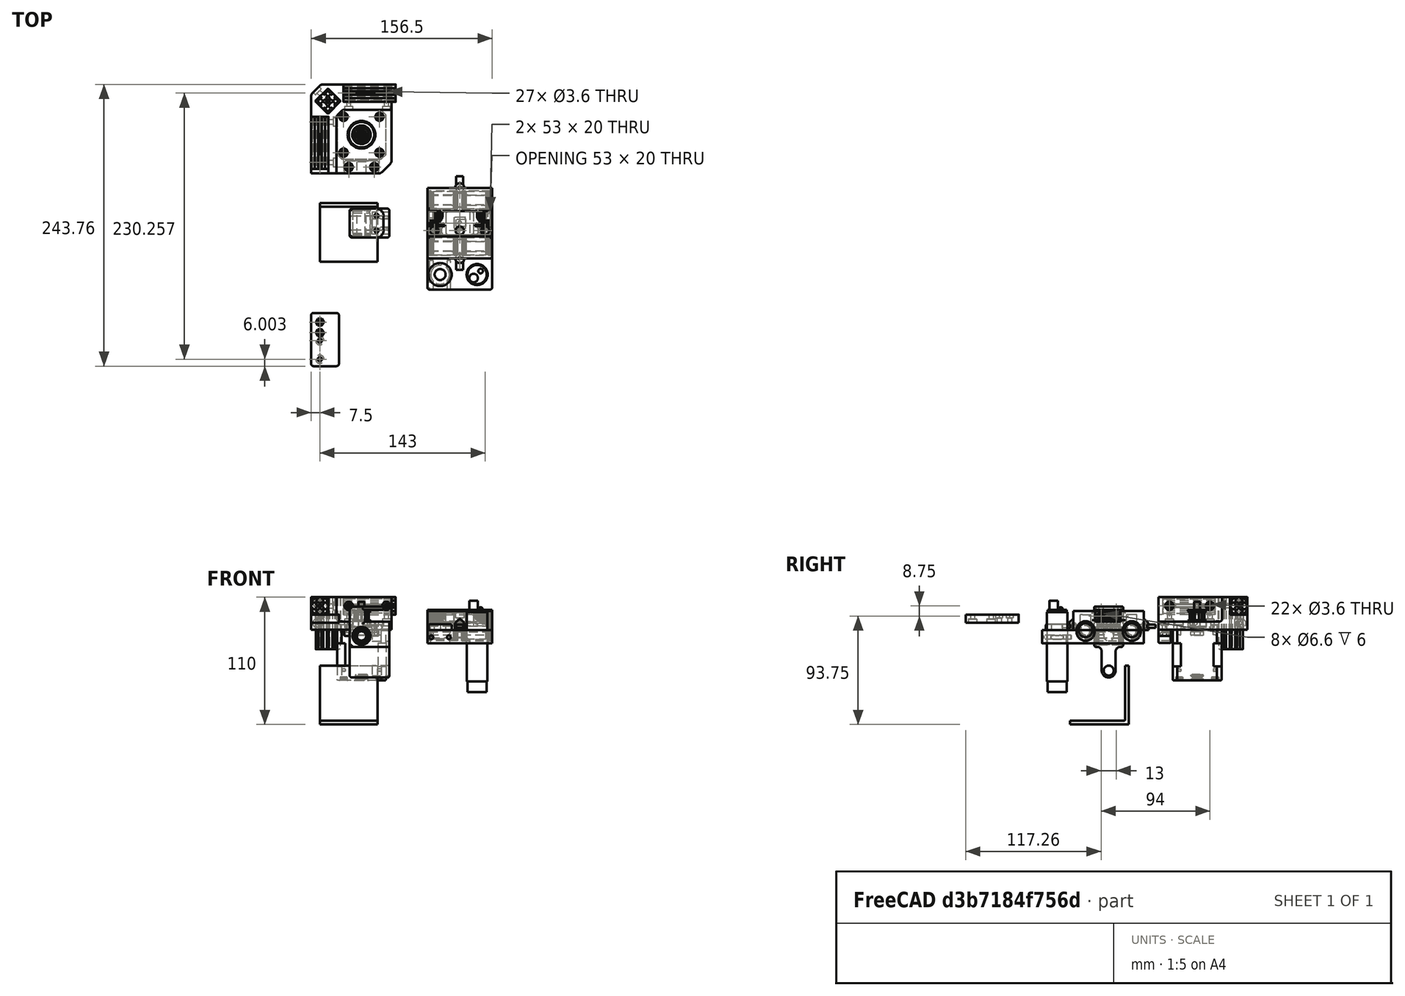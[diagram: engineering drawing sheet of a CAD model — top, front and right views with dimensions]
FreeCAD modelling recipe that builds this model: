
FCSTD DOCUMENT  (FreeCAD 0.15R4671 (Git))
Label: XCarrageTop
License: All rights reserved
LicenseURL: http://en.wikipedia.org/wiki/All_rights_reserved
objects: Sketcher::SketchObject×26, Mesh::Feature×24, Part::Feature×21, PartDesign::Pocket×20, PartDesign::Fillet×10, PartDesign::Pad×6, PartDesign::Chamfer×2
note: 111 computed .brp shape members not serialized (recipe doc carries the construction recipe); baked Part::Feature solids carry a one-line shape summary decoded from their .brp

FEATURE [Part::Feature] Part__Feature  label="OB1515_45mm001"
  Placement = pos=(0,79.5,22.5) rot=(1,0,0;1.5708rad)
  shape: bbox 15 x 45 x 15 mm, 158 faces (baked)
FEATURE [Part::Feature] Part__Feature001  label="OB1515_45mm"
  Placement = pos=(7,93,-15) rot=(0,0,1;0.785398rad)
  shape: bbox 21.01 x 21.01 x 45 mm, 158 faces (baked)
FEATURE [Part::Feature] Part__Feature002  label="OB1515_45mm002"
  Placement = pos=(20.5,100,22.5) rot=(0.57735,0.57735,0.57735;2.0944rad)
  shape: bbox 45 x 15 x 15 mm, 158 faces (baked)
FEATURE [Part::Feature] Part__Feature003  label="NEMA17"
  Placement = pos=(36,64,2) rot=(0,0,1;0rad)
  shape: bbox 42.3 x 42.3 x 68 mm, 275 faces (baked)
FEATURE [Part::Feature] Part__Feature004  label="T5_Pulley"
  Placement = pos=(36,64,-4) rot=(0,0,1;0rad)
  shape: bbox 16 x 16 x 14.8 mm, 116 faces (baked)
FEATURE [Mesh::Feature] _08ZZ_Ball_Bearing  label="608ZZ_Ball_Bearing001"
  Placement = pos=(54.5,64,25.1) rot=(0,0,1;0rad)
FEATURE [Mesh::Feature] Spacer
  Placement = pos=(21.5,54,17.6) rot=(0,0,1;0rad)
FEATURE [Mesh::Feature] _mmRod_x100mm  label="8mmRod_x100mm"
  Placement = pos=(36,-64.5,-3.5) rot=(0,0,1;3.14159rad)
FEATURE [Part::Feature] Part__Feature005  label="TopCornerMotor"
  Placement = pos=(0,100,0) rot=(0,0,1;0rad)
  shape: bbox 69.55 x 77 x 28 mm, 82 faces (baked)
FEATURE [Part::Feature] Part__Feature006  label="TopRodHolder"
  Placement = pos=(0,100,2) rot=(0,0,1;0rad)
  shape: bbox 30.16 x 11.33 x 11.99 mm, 58 faces (baked)
FEATURE [Part::Feature] LM8UU_8mm_Linear_Bearing001
  Placement = pos=(36,-24.5,-3.5) rot=(0,0,1;1.5708rad)
  shape: bbox 15 x 24 x 15 mm, 34 faces (baked)
FEATURE [Mesh::Feature] _mmRod_x100mm001  label="8mmRod_x100mm001"
  Placement = pos=(45,7.5,1.5) rot=(0,0,1;1.5708rad)
FEATURE [Mesh::Feature] _mmRod_x100mm002  label="8mmRod_x100mm002"
  Placement = pos=(45,-32.5,1.5) rot=(0,0,1;1.5708rad)
FEATURE [Mesh::Feature] _0mmFan  label="40mmFan"
  Placement = pos=(102,-18,-36) rot=(-1,0,0;1.5708rad)
FEATURE [Mesh::Feature] HexHotEnd  label="HexHotEnd1"
  Placement = pos=(104,-57,-34) rot=(0,0,1;0rad)
FEATURE [Mesh::Feature] HexNutStyle1_M  label="HexNutStyle1_M007"
  Placement = pos=(1.3,-81.1,-104) rot=(0,0,1;0.523599rad)
FEATURE [Mesh::Feature] HexNutStyle1_M001  label="HexNutStyle1_M3"
  Placement = pos=(1.3,-72.1,-104) rot=(0,0,1;0.523599rad)
FEATURE [Part::Feature] Part__Feature007  label="CableChain2OpenBeamBracket"
  Placement = pos=(0,-17,-7) rot=(0,0,1;0rad)
  shape: bbox 24 x 46 x 7 mm, 32 faces (baked)
FEATURE [Mesh::Feature] PNEUMATIC_NIPPLE
  Placement = pos=(111,-50,-28) rot=(0,-1,0;1.5708rad)
FEATURE [Part::Feature] Part__Feature015  label="AluAngle"
  Placement = pos=(0,5,-80) rot=(-1,0,0;1.5708rad)
  shape: bbox 50 x 50.8 x 50.8 mm, 9 faces (baked)
FEATURE [Mesh::Feature] _x10x4_FlangedBearing  label="5x10x4_FlangedBearing_BOTTOM"
  Placement = pos=(49,-6,16) rot=(-1,0,0;1.5708rad)
FEATURE [Mesh::Feature] _x10x4_FlangedBearing001  label="5x10x4_FlangedBearing_TOP"
  Placement = pos=(49,-6,12) rot=(1,0,0;1.5708rad)
FEATURE [Mesh::Feature] _x10x4_FlangedBearing002  label="5x10x4_FlangedBearing_BOTTOM001"
  Placement = pos=(49,-19,16) rot=(-1,0,0;1.5708rad)
FEATURE [Mesh::Feature] _x10x4_FlangedBearing003  label="5x10x4_FlangedBearing_TOP001"
  Placement = pos=(49,-19,12) rot=(1,0,0;1.5708rad)
FEATURE [Part::Feature] Part__Feature016  label="XCarrageBeltBlock"
  Placement = pos=(9,0,0) rot=(0,0,1;0rad)
  shape: bbox 56 x 22 x 10 mm, 113 faces (baked)
FEATURE [Part::Feature] Part__Feature017  label="LJ18A3"
  Placement = pos=(136,-57,-52) rot=(0,0,1;0rad)
  shape: bbox 17.85 x 17.85 x 79.1 mm, 11 faces (baked)
FEATURE [Mesh::Feature] HexNutStyle1_M002  label="HexNutStyle1_M008"
  Placement = pos=(50.3,7.15,-114) rot=(0,0,1;0.523599rad)
FEATURE [Mesh::Feature] HexNutStyle1_M003  label="HexNutStyle1_M009"
  Placement = pos=(50.3,20.15,-114) rot=(0,0,1;0.523599rad)
FEATURE [Part::Feature] Part__Feature018  label="YCarrage"
  shape: bbox 34.23 x 25.99 x 62.01 mm, 85 faces (baked)
FEATURE [Part::Feature] LM8UU_8mm_Linear_Bearing
  Placement = pos=(95,7.5,1.5) rot=(-1,0,0;1.5708rad)
  shape: bbox 24 x 15 x 15 mm, 34 faces (baked)
FEATURE [Part::Feature] LM8UU_8mm_Linear_Bearing002
  Placement = pos=(95,-32.5,1.5) rot=(-1,0,0;1.5708rad)
  shape: bbox 24 x 15 x 15 mm, 34 faces (baked)
FEATURE [Part::Feature] LM8UU_8mm_Linear_Bearing003
  Placement = pos=(123,7.5,1.5) rot=(-1,0,0;1.5708rad)
  shape: bbox 24 x 15 x 15 mm, 34 faces (baked)
FEATURE [Part::Feature] LM8UU_8mm_Linear_Bearing004
  Placement = pos=(123,-32.5,1.5) rot=(-1,0,0;1.5708rad)
  shape: bbox 24 x 15 x 15 mm, 34 faces (baked)
FEATURE [Mesh::Feature] MicroSwitch
  Placement = pos=(99,-12.5,-5) rot=(0,0,1;1.5708rad)
FEATURE [Sketcher::SketchObject] Sketch
  Placement = pos=(0,0,1.5) rot=(0,0,1;0rad)
  sketch-geometry (4):
    g0: LineSegment StartX=93 StartY=18 StartZ=0 EndX=149 EndY=18 EndZ=0
    g1: LineSegment StartX=149 StartY=18 StartZ=0 EndX=149 EndY=-43 EndZ=0
    g2: LineSegment StartX=149 StartY=-43 StartZ=0 EndX=93 EndY=-43 EndZ=0
    g3: LineSegment StartX=93 StartY=-43 StartZ=0 EndX=93 EndY=18 EndZ=0
  constraints (8):
    c: Coincident(g0,g1)
    c: Coincident(g1,g2)
    c: Coincident(g2,g3)
    c: Coincident(g3,g0)
    c: Horizontal(g0)
    c: Horizontal(g2)
    c: Vertical(g1)
    c: Vertical(g3)
FEATURE [Part::Feature] Part__Feature019  label="BottomHalf"
  shape: bbox 57.67 x 88 x 16.5 mm, 58 faces (baked)
FEATURE [PartDesign::Pad] Pad
  Length = 16.5
  Length2 = 100
  Placement = pos=(0,0,1.5) rot=(0,0,1;0rad)
  Sketch = -> Sketch
  Type = 0
FEATURE [Sketcher::SketchObject] Sketch001
  Placement = pos=(149,0,1.5) rot=(0.57735,0.57735,0.57735;2.0944rad)
  Support = -> Pad [Face2]
  sketch-geometry (2):
    g0: Circle CenterX=-32.5 CenterY=0 CenterZ=0 NormalX=0 NormalY=0 NormalZ=1 Radius=7.75
    g1: Circle CenterX=7.5 CenterY=0 CenterZ=0 NormalX=0 NormalY=0 NormalZ=1 Radius=7.75
  constraints (2):
    c: Radius(g1) = 7.75
    c: Radius(g0) = 7.75
FEATURE [PartDesign::Pocket] Pocket
  Length = 26.25
  Placement = pos=(0,0,1.5) rot=(0,0,1;0rad)
  Sketch = -> Sketch001
  Type = 0
FEATURE [Sketcher::SketchObject] Sketch002
  Placement = pos=(93,0,1.5) rot=(0.57735,-0.57735,-0.57735;2.0944rad)
  Support = -> Pocket [Face2]
  sketch-geometry (2):
    g0: Circle CenterX=32.5 CenterY=0 CenterZ=0 NormalX=0 NormalY=0 NormalZ=1 Radius=7.75
    g1: Circle CenterX=-7.5 CenterY=0 CenterZ=0 NormalX=0 NormalY=0 NormalZ=1 Radius=7.75
  constraints (2):
    c: Radius(g1) = 7.75
    c: Radius(g0) = 7.75
FEATURE [PartDesign::Pocket] Pocket001
  Length = 26.25
  Placement = pos=(0,0,1.5) rot=(0,0,1;0rad)
  Sketch = -> Sketch002
  Type = 0
FEATURE [Sketcher::SketchObject] Sketch003
  Placement = pos=(93,0,1.5) rot=(0.57735,-0.57735,-0.57735;2.0944rad)
  Support = -> Pocket001 [Face2]
  sketch-geometry (4):
    g0: LineSegment StartX=-15.5 StartY=0 StartZ=0 EndX=40.5 EndY=0 EndZ=0
    g1: LineSegment StartX=40.5 StartY=0 StartZ=0 EndX=40.5 EndY=8 EndZ=0
    g2: LineSegment StartX=40.5 StartY=8 StartZ=0 EndX=-15.5 EndY=8 EndZ=0
    g3: LineSegment StartX=-15.5 StartY=8 StartZ=0 EndX=-15.5 EndY=0 EndZ=0
  constraints (8):
    c: Coincident(g0,g1)
    c: Coincident(g1,g2)
    c: Coincident(g2,g3)
    c: Coincident(g3,g0)
    c: Horizontal(g0)
    c: Horizontal(g2)
    c: Vertical(g1)
    c: Vertical(g3)
FEATURE [PartDesign::Pad] Pad001
  Length = 1.25
  Length2 = 100
  Placement = pos=(0,0,1.5) rot=(0,0,1;0rad)
  Reversed = true
  Sketch = -> Sketch003
  Type = 0
FEATURE [Sketcher::SketchObject] Sketch004
  Placement = pos=(149,0,1.5) rot=(0.57735,0.57735,0.57735;2.0944rad)
  Support = -> Pad001 [Face2]
  sketch-geometry (4):
    g0: LineSegment StartX=-40.5 StartY=0 StartZ=0 EndX=15.5 EndY=0 EndZ=0
    g1: LineSegment StartX=15.5 StartY=0 StartZ=0 EndX=15.5 EndY=8 EndZ=0
    g2: LineSegment StartX=15.5 StartY=8 StartZ=0 EndX=-40.5 EndY=8 EndZ=0
    g3: LineSegment StartX=-40.5 StartY=8 StartZ=0 EndX=-40.5 EndY=0 EndZ=0
  constraints (8):
    c: Coincident(g0,g1)
    c: Coincident(g1,g2)
    c: Coincident(g2,g3)
    c: Coincident(g3,g0)
    c: Horizontal(g0)
    c: Horizontal(g2)
    c: Vertical(g1)
    c: Vertical(g3)
FEATURE [PartDesign::Pad] Pad002
  Length = 1.25
  Length2 = 100
  Placement = pos=(0,0,1.5) rot=(0,0,1;0rad)
  Reversed = true
  Sketch = -> Sketch004
  Type = 0
FEATURE [Sketcher::SketchObject] Sketch005
  Placement = pos=(149,0,1.5) rot=(0.57735,0.57735,0.57735;2.0944rad)
  Support = -> Pad002 [Face5]
  sketch-geometry (2):
    g0: Circle CenterX=7.5 CenterY=0 CenterZ=0 NormalX=0 NormalY=0 NormalZ=1 Radius=6
    g1: Circle CenterX=-32.5 CenterY=0 CenterZ=0 NormalX=0 NormalY=0 NormalZ=1 Radius=6
  constraints (2):
    c: Radius(g0) = 6
    c: Radius(g1) = 6
FEATURE [PartDesign::Pocket] Pocket002
  Length = 5
  Placement = pos=(0,0,1.5) rot=(0,0,1;0rad)
  Sketch = -> Sketch005
  Type = 1
FEATURE [PartDesign::Fillet] Fillet
  Base = -> Pocket002 [Edge2,Edge1,Edge29,Edge17]
  Placement = pos=(0,0,1.5) rot=(0,0,1;0rad)
  Radius = 2
FEATURE [Sketcher::SketchObject] Sketch006
  Placement = pos=(0,0,18) rot=(0,0,1;0rad)
  Support = -> Fillet [Face5]
  sketch-geometry (32):
    g0: ArcOfCircle CenterX=100.5 CenterY=-6 CenterZ=0 NormalX=0 NormalY=0 NormalZ=1 Radius=6 StartAngle=4.71239 EndAngle=7.85398
    g1: ArcOfCircle CenterX=100.5 CenterY=-6 CenterZ=0 NormalX=0 NormalY=0 NormalZ=1 Radius=4.5 StartAngle=4.71239 EndAngle=7.85398
    g2: ArcOfCircle CenterX=141.5 CenterY=-6 CenterZ=0 NormalX=0 NormalY=0 NormalZ=1 Radius=6 StartAngle=1.5708 EndAngle=4.71239
    g3: ArcOfCircle CenterX=141.5 CenterY=-6 CenterZ=0 NormalX=0 NormalY=0 NormalZ=1 Radius=4.5 StartAngle=1.5708 EndAngle=4.71239
    g4: LineSegment StartX=100.5 StartY=0 StartZ=0 EndX=92 EndY=0 EndZ=0
    g5: LineSegment StartX=92 StartY=0 StartZ=0 EndX=92 EndY=-1.5 EndZ=0
    g6: LineSegment StartX=92 StartY=-1.5 StartZ=0 EndX=100.5 EndY=-1.5 EndZ=0
    g7: LineSegment StartX=141.5 StartY=0 StartZ=0 EndX=150 EndY=0 EndZ=0
    g8: LineSegment StartX=150 StartY=0 StartZ=0 EndX=150 EndY=-1.5 EndZ=0
    g9: LineSegment StartX=150 StartY=-1.5 StartZ=0 EndX=141.5 EndY=-1.5 EndZ=0
    g10: LineSegment StartX=100.5 StartY=-10.5 StartZ=0 EndX=92 EndY=-10.5 EndZ=0
    g11: LineSegment StartX=92 StartY=-10.5 StartZ=0 EndX=92 EndY=-12 EndZ=0
    g12: LineSegment StartX=92 StartY=-12 StartZ=0 EndX=100.5 EndY=-12 EndZ=0
    g13: LineSegment StartX=141.5 StartY=-10.5 StartZ=0 EndX=150 EndY=-10.5 EndZ=0
    g14: LineSegment StartX=150 StartY=-10.5 StartZ=0 EndX=150 EndY=-12 EndZ=0
    g15: LineSegment StartX=150 StartY=-12 StartZ=0 EndX=141.5 EndY=-12 EndZ=0
    g16: LineSegment StartX=92 StartY=-13 StartZ=0 EndX=100.5 EndY=-13 EndZ=0
    g17: LineSegment StartX=100.5 StartY=-14.5 StartZ=0 EndX=92 EndY=-14.5 EndZ=0
    g18: LineSegment StartX=92 StartY=-14.5 StartZ=0 EndX=92 EndY=-13 EndZ=0
    g19: LineSegment StartX=141.5 StartY=-13 StartZ=0 EndX=150 EndY=-13 EndZ=0
    g20: LineSegment StartX=150 StartY=-13 StartZ=0 EndX=150 EndY=-14.5 EndZ=0
    g21: LineSegment StartX=150 StartY=-14.5 StartZ=0 EndX=141.5 EndY=-14.5 EndZ=0
    g22: ArcOfCircle CenterX=141.5 CenterY=-19 CenterZ=0 NormalX=0 NormalY=0 NormalZ=1 Radius=4.5 StartAngle=1.5708 EndAngle=4.71239
    g23: ArcOfCircle CenterX=141.5 CenterY=-19 CenterZ=0 NormalX=0 NormalY=0 NormalZ=1 Radius=6 StartAngle=1.5708 EndAngle=4.71239
    g24: ArcOfCircle CenterX=100.5 CenterY=-19 CenterZ=0 NormalX=0 NormalY=0 NormalZ=1 Radius=4.5 StartAngle=4.71239 EndAngle=7.85398
    g25: ArcOfCircle CenterX=100.5 CenterY=-19 CenterZ=0 NormalX=0 NormalY=0 NormalZ=1 Radius=6 StartAngle=4.71239 EndAngle=7.85398
    g26: LineSegment StartX=100.5 StartY=-23.5 StartZ=0 EndX=92 EndY=-23.5 EndZ=0
    g27: LineSegment StartX=92 StartY=-23.5 StartZ=0 EndX=92 EndY=-25 EndZ=0
    g28: LineSegment StartX=92 StartY=-25 StartZ=0 EndX=100.5 EndY=-25 EndZ=0
    g29: LineSegment StartX=141.5 StartY=-23.5 StartZ=0 EndX=150 EndY=-23.5 EndZ=0
    g30: LineSegment StartX=150 StartY=-23.5 StartZ=0 EndX=150 EndY=-25 EndZ=0
    g31: LineSegment StartX=150 StartY=-25 StartZ=0 EndX=141.5 EndY=-25 EndZ=0
  constraints (64):
    c: Coincident(g4,g5)
    c: Coincident(g5,g6)
    c: Horizontal(g4)
    c: Horizontal(g6)
    c: Vertical(g5)
    c: Coincident(g7,g8)
    c: Coincident(g8,g9)
    c: Horizontal(g7)
    c: Horizontal(g9)
    c: Vertical(g8)
    c: Coincident(g10,g11)
    c: Coincident(g11,g12)
    c: Horizontal(g10)
    c: Horizontal(g12)
    c: Vertical(g11)
    c: Coincident(g13,g14)
    c: Coincident(g14,g15)
    c: Horizontal(g13)
    c: Horizontal(g15)
    c: Vertical(g14)
    c: Coincident(g17,g18)
    c: Coincident(g18,g16)
    c: Horizontal(g16)
    c: Horizontal(g17)
    c: Vertical(g18)
    c: Coincident(g19,g20)
    c: Coincident(g20,g21)
    c: Horizontal(g19)
    c: Horizontal(g21)
    c: Vertical(g20)
    c: Radius(g3) = 4.5
    c: Radius(g1) = 4.5
    c: Radius(g2) = 6
    c: Radius(g0) = 6
    c: Coincident(g26,g27)
    c: Coincident(g27,g28)
    c: Horizontal(g26)
    c: Horizontal(g28)
    c: Vertical(g27)
    c: Coincident(g29,g30)
    c: Coincident(g30,g31)
    c: Horizontal(g29)
    c: Horizontal(g31)
    c: Vertical(g30)
    c: Radius(g24) = 4.5
    c: Radius(g22) = 4.5
    c: Radius(g23) = 6
    c: Radius(g25) = 6
    c: Coincident(g22,g29)
    c: Coincident(g23,g31)
    c: Coincident(g21,g22)
    c: Coincident(g19,g23)
    c: Coincident(g2,g15)
    c: Coincident(g3,g13)
    c: Coincident(g3,g9)
    c: Coincident(g2,g7)
    c: Coincident(g0,g4)
    c: Coincident(g1,g6)
    c: Coincident(g1,g10)
    c: Coincident(g0,g12)
    c: Coincident(g17,g24)
    c: Coincident(g24,g26)
    c: Coincident(g25,g28)
    c: Coincident(g16,g25)
FEATURE [PartDesign::Pocket] Pocket003
  Length = 8
  Placement = pos=(0,0,1.5) rot=(0,0,1;0rad)
  Sketch = -> Sketch006
  Type = 0
FEATURE [PartDesign::Fillet] Fillet001
  Base = -> Pocket003 [Edge44,Edge159,Edge167,Edge40,Edge32,Edge176,Edge28,Edge184]
  Placement = pos=(0,0,1.5) rot=(0,0,1;0rad)
  Radius = 0.4
FEATURE [PartDesign::Fillet] Fillet002
  Base = -> Fillet001 [Edge7,Edge18,Edge80,Edge102,Edge35,Edge57]
  Placement = pos=(0,0,1.5) rot=(0,0,1;0rad)
  Radius = 2
FEATURE [Sketcher::SketchObject] Sketch007
  Placement = pos=(0,0,1.5) rot=(1,0,0;3.14159rad)
  Support = -> Fillet002 [Face35]
  sketch-geometry (4):
    g0: LineSegment StartX=94.5 StartY=22.5 StartZ=0 EndX=147.5 EndY=22.5 EndZ=0
    g1: LineSegment StartX=147.5 StartY=22.5 StartZ=0 EndX=147.5 EndY=2.5 EndZ=0
    g2: LineSegment StartX=147.5 StartY=2.5 StartZ=0 EndX=94.5 EndY=2.5 EndZ=0
    g3: LineSegment StartX=94.5 StartY=2.5 StartZ=0 EndX=94.5 EndY=22.5 EndZ=0
  constraints (8):
    c: Coincident(g0,g1)
    c: Coincident(g1,g2)
    c: Coincident(g2,g3)
    c: Coincident(g3,g0)
    c: Horizontal(g0)
    c: Horizontal(g2)
    c: Vertical(g1)
    c: Vertical(g3)
FEATURE [PartDesign::Pocket] Pocket004
  Length = 5
  Placement = pos=(0,0,1.5) rot=(0,0,1;0rad)
  Sketch = -> Sketch007
  Type = 0
FEATURE [Sketcher::SketchObject] Sketch008
  Placement = pos=(0,0,6.5) rot=(1,0,0;3.14159rad)
  Support = -> Pocket004 [Face120]
  sketch-geometry (4):
    g0: LineSegment StartX=109 StartY=22.5 StartZ=0 EndX=133 EndY=22.5 EndZ=0
    g1: LineSegment StartX=133 StartY=22.5 StartZ=0 EndX=133 EndY=2.5 EndZ=0
    g2: LineSegment StartX=133 StartY=2.5 StartZ=0 EndX=109 EndY=2.5 EndZ=0
    g3: LineSegment StartX=109 StartY=2.5 StartZ=0 EndX=109 EndY=22.5 EndZ=0
  constraints (8):
    c: Coincident(g0,g1)
    c: Coincident(g1,g2)
    c: Coincident(g2,g3)
    c: Coincident(g3,g0)
    c: Horizontal(g0)
    c: Horizontal(g2)
    c: Vertical(g1)
    c: Vertical(g3)
FEATURE [PartDesign::Pocket] Pocket005
  Length = 10
  Placement = pos=(0,0,1.5) rot=(0,0,1;0rad)
  Sketch = -> Sketch008
  Type = 0
FEATURE [Part::Feature] Pocket006
  shape: bbox 56 x 61 x 16.52 mm, 133 faces (baked)
FEATURE [PartDesign::Fillet] Fillet003
  Base = -> Pocket006 [Edge349,Edge351]
  Radius = 4
FEATURE [Sketcher::SketchObject] Sketch009
  Placement = pos=(0,0,1.5) rot=(1,0,0;3.14159rad)
  Support = -> Fillet003 [Face41]
  sketch-geometry (16):
    g0: LineSegment StartX=97 StartY=37 StartZ=0 EndX=116 EndY=37 EndZ=0
    g1: LineSegment StartX=116 StartY=37 StartZ=0 EndX=116 EndY=28 EndZ=0
    g2: LineSegment StartX=116 StartY=28 StartZ=0 EndX=97 EndY=28 EndZ=0
    g3: LineSegment StartX=97 StartY=28 StartZ=0 EndX=97 EndY=37 EndZ=0
    g4: LineSegment StartX=126 StartY=28 StartZ=0 EndX=145 EndY=28 EndZ=0
    g5: LineSegment StartX=145 StartY=28 StartZ=0 EndX=145 EndY=37 EndZ=0
    g6: LineSegment StartX=145 StartY=37 StartZ=0 EndX=126 EndY=37 EndZ=0
    g7: LineSegment StartX=126 StartY=37 StartZ=0 EndX=126 EndY=28 EndZ=0
    g8: LineSegment StartX=97 StartY=-3 StartZ=0 EndX=116 EndY=-3 EndZ=0
    g9: LineSegment StartX=116 StartY=-3 StartZ=0 EndX=116 EndY=-12 EndZ=0
    g10: LineSegment StartX=116 StartY=-12 StartZ=0 EndX=97 EndY=-12 EndZ=0
    g11: LineSegment StartX=97 StartY=-12 StartZ=0 EndX=97 EndY=-3 EndZ=0
    g12: LineSegment StartX=126 StartY=-3 StartZ=0 EndX=145 EndY=-3 EndZ=0
    g13: LineSegment StartX=145 StartY=-3 StartZ=0 EndX=145 EndY=-12 EndZ=0
    g14: LineSegment StartX=145 StartY=-12 StartZ=0 EndX=126 EndY=-12 EndZ=0
    g15: LineSegment StartX=126 StartY=-12 StartZ=0 EndX=126 EndY=-3 EndZ=0
  constraints (32):
    c: Coincident(g0,g1)
    c: Coincident(g1,g2)
    c: Coincident(g2,g3)
    c: Coincident(g3,g0)
    c: Horizontal(g0)
    c: Horizontal(g2)
    c: Vertical(g1)
    c: Vertical(g3)
    c: Coincident(g4,g5)
    c: Coincident(g5,g6)
    c: Coincident(g6,g7)
    c: Coincident(g7,g4)
    c: Horizontal(g4)
    c: Horizontal(g6)
    c: Vertical(g5)
    c: Vertical(g7)
    c: Coincident(g8,g9)
    c: Coincident(g9,g10)
    c: Coincident(g10,g11)
    c: Coincident(g11,g8)
    c: Horizontal(g8)
    c: Horizontal(g10)
    c: Vertical(g9)
    c: Vertical(g11)
    c: Coincident(g12,g13)
    c: Coincident(g13,g14)
    c: Coincident(g14,g15)
    c: Coincident(g15,g12)
    c: Horizontal(g12)
    c: Horizontal(g14)
    c: Vertical(g13)
    c: Vertical(g15)
FEATURE [PartDesign::Pocket] Pocket007
  Length = 13.5
  Sketch = -> Sketch009
  Type = 0
FEATURE [PartDesign::Fillet] Fillet004
  Base = -> Pocket007 [Edge329,Edge323,Edge260,Edge254,Edge262,Edge325,Edge268,Edge251,Edge257,Edge252,Edge267,Edge327,Edge259,Edge270,Edge249,Edge265]
  Radius = 2
FEATURE [PartDesign::Fillet] Fillet005
  Base = -> Fillet004 [Edge197,Edge200,Edge187,Edge190]
  Radius = 2
FEATURE [PartDesign::Fillet] Fillet006
  Base = -> Fillet005 [Edge155,Edge151,Edge125,Edge122]
  Radius = 1
FEATURE [Part::Feature] Fillet007
  shape: bbox 56 x 61 x 16.52 mm, 187 faces (baked)
FEATURE [Sketcher::SketchObject] Sketch010
  Placement = pos=(0,0,1.5) rot=(1,0,0;3.14159rad)
  Support = -> Fillet007 [Face30]
  sketch-geometry (8):
    g0: ArcOfCircle CenterX=121 CenterY=-18 CenterZ=0 NormalX=0 NormalY=0 NormalZ=1 Radius=4 StartAngle=3.14159 EndAngle=6.28319
    g1: ArcOfCircle CenterX=121 CenterY=43 CenterZ=0 NormalX=0 NormalY=0 NormalZ=1 Radius=4 StartAngle=0 EndAngle=3.14159
    g2: LineSegment StartX=117 StartY=43 StartZ=0 EndX=117 EndY=41 EndZ=0
    g3: LineSegment StartX=117 StartY=41 StartZ=0 EndX=125 EndY=41 EndZ=0
    g4: LineSegment StartX=125 StartY=41 StartZ=0 EndX=125 EndY=43 EndZ=0
    g5: LineSegment StartX=125 StartY=-18 StartZ=0 EndX=125 EndY=-16 EndZ=0
    g6: LineSegment StartX=125 StartY=-16 StartZ=0 EndX=117 EndY=-16 EndZ=0
    g7: LineSegment StartX=117 StartY=-16 StartZ=0 EndX=117 EndY=-18 EndZ=0
  constraints (10):
    c: Coincident(g2,g3)
    c: Coincident(g3,g4)
    c: Radius(g1) = 4
    c: Coincident(g5,g6)
    c: Coincident(g6,g7)
    c: Radius(g0) = 4
    c: Coincident(g0,g5)
    c: Coincident(g0,g7)
    c: Coincident(g1,g4)
    c: Coincident(g1,g2)
FEATURE [Mesh::Feature] HexNutStyle1_M004  label="HexNutStyle1_M010"
  Placement = pos=(135.2,40,-113) rot=(0,0,1;0rad)
FEATURE [Mesh::Feature] HexNutStyle1_M005  label="HexNutStyle1_M011"
  Placement = pos=(135.2,-21,-113) rot=(0,0,1;0rad)
FEATURE [PartDesign::Pad] Pad003
  Length = 10
  Length2 = 100
  Reversed = true
  Sketch = -> Sketch010
  Type = 0
FEATURE [PartDesign::Chamfer] Chamfer
  Base = -> Pad003 [Edge510]
  Size = 3.99
FEATURE [PartDesign::Chamfer] Chamfer001
  Base = -> Chamfer [Edge409]
  Size = 3.99
FEATURE [PartDesign::Fillet] Fillet008
  Base = -> Chamfer001 [Edge11,Edge411]
  Radius = 2
FEATURE [Sketcher::SketchObject] Sketch011
  Placement = pos=(0,18,0) rot=(0,0.707107,0.707107;3.14159rad)
  Support = -> Fillet008 [Face112]
  sketch-geometry (4):
    g0: LineSegment StartX=-124 StartY=6.25 StartZ=0 EndX=-118 EndY=6.25 EndZ=0
    g1: LineSegment StartX=-118 StartY=6.25 StartZ=0 EndX=-118 EndY=3.5 EndZ=0
    g2: LineSegment StartX=-118 StartY=3.5 StartZ=0 EndX=-124 EndY=3.5 EndZ=0
    g3: LineSegment StartX=-124 StartY=3.5 StartZ=0 EndX=-124 EndY=6.25 EndZ=0
  constraints (8):
    c: Coincident(g0,g1)
    c: Coincident(g1,g2)
    c: Coincident(g2,g3)
    c: Coincident(g3,g0)
    c: Horizontal(g0)
    c: Horizontal(g2)
    c: Vertical(g1)
    c: Vertical(g3)
FEATURE [Sketcher::SketchObject] Sketch012
  Placement = pos=(0,0,1.5) rot=(1,0,0;3.14159rad)
  Support = -> Fillet008 [Face4]
  sketch-geometry (2):
    g0: Circle CenterX=121 CenterY=43 CenterZ=0 NormalX=0 NormalY=0 NormalZ=1 Radius=1.8
    g1: Circle CenterX=121 CenterY=-18 CenterZ=0 NormalX=0 NormalY=0 NormalZ=1 Radius=1.8
  constraints (2):
    c: Radius(g1) = 1.8
    c: Radius(g0) = 1.8
FEATURE [PartDesign::Pocket] Pocket008
  Length = 6
  Sketch = -> Sketch012
  Type = 0
FEATURE [PartDesign::Pocket] Pocket009
  Length = 10
  Reversed = true
  Sketch = -> Sketch011
  Type = 0
FEATURE [Sketcher::SketchObject] Sketch013
  Placement = pos=(0,18,0) rot=(0,0.707107,0.707107;3.14159rad)
  Support = -> Pocket009 [Face200]
  sketch-geometry (4):
    g0: LineSegment StartX=-124 StartY=6.25 StartZ=0 EndX=-118 EndY=6.25 EndZ=0
    g1: LineSegment StartX=-118 StartY=6.25 StartZ=0 EndX=-118 EndY=3.5 EndZ=0
    g2: LineSegment StartX=-118 StartY=3.5 StartZ=0 EndX=-124 EndY=3.5 EndZ=0
    g3: LineSegment StartX=-124 StartY=3.5 StartZ=0 EndX=-124 EndY=6.25 EndZ=0
  constraints (8):
    c: Coincident(g0,g1)
    c: Coincident(g1,g2)
    c: Coincident(g2,g3)
    c: Coincident(g3,g0)
    c: Horizontal(g0)
    c: Horizontal(g2)
    c: Vertical(g1)
    c: Vertical(g3)
FEATURE [PartDesign::Pocket] Pocket010
  Length = 3.5
  Sketch = -> Sketch013
  Type = 0
FEATURE [Sketcher::SketchObject] Sketch014
  Placement = pos=(0,-43,0) rot=(1,0,0;1.5708rad)
  Support = -> Pocket010 [Face1]
  sketch-geometry (4):
    g0: LineSegment StartX=118 StartY=6.25 StartZ=0 EndX=124 EndY=6.25 EndZ=0
    g1: LineSegment StartX=124 StartY=6.25 StartZ=0 EndX=124 EndY=3.5 EndZ=0
    g2: LineSegment StartX=124 StartY=3.5 StartZ=0 EndX=118 EndY=3.5 EndZ=0
    g3: LineSegment StartX=118 StartY=3.5 StartZ=0 EndX=118 EndY=6.25 EndZ=0
  constraints (8):
    c: Coincident(g0,g1)
    c: Coincident(g1,g2)
    c: Coincident(g2,g3)
    c: Coincident(g3,g0)
    c: Horizontal(g0)
    c: Horizontal(g2)
    c: Vertical(g1)
    c: Vertical(g3)
FEATURE [PartDesign::Pocket] Pocket011
  Length = 10
  Reversed = true
  Sketch = -> Sketch014
  Type = 0
FEATURE [Sketcher::SketchObject] Sketch015
  Placement = pos=(0,-43,0) rot=(1,0,0;1.5708rad)
  Support = -> Pocket011 [Face30]
  sketch-geometry (4):
    g0: LineSegment StartX=118 StartY=6.25 StartZ=0 EndX=124 EndY=6.25 EndZ=0
    g1: LineSegment StartX=124 StartY=6.25 StartZ=0 EndX=124 EndY=3.5 EndZ=0
    g2: LineSegment StartX=124 StartY=3.5 StartZ=0 EndX=118 EndY=3.5 EndZ=0
    g3: LineSegment StartX=118 StartY=3.5 StartZ=0 EndX=118 EndY=6.25 EndZ=0
  constraints (8):
    c: Coincident(g0,g1)
    c: Coincident(g1,g2)
    c: Coincident(g2,g3)
    c: Coincident(g3,g0)
    c: Horizontal(g0)
    c: Horizontal(g2)
    c: Vertical(g1)
    c: Vertical(g3)
FEATURE [PartDesign::Pocket] Pocket012
  Length = 3.5
  Sketch = -> Sketch015
  Type = 0
FEATURE [Sketcher::SketchObject] Sketch016
  Placement = pos=(0,0,16.5) rot=(1,0,0;3.14159rad)
  Support = -> Pocket012 [Face169]
  sketch-geometry (4):
    g0: LineSegment StartX=116 StartY=17.5 StartZ=0 EndX=126 EndY=17.5 EndZ=0
    g1: LineSegment StartX=126 StartY=17.5 StartZ=0 EndX=126 EndY=7.5 EndZ=0
    g2: LineSegment StartX=126 StartY=7.5 StartZ=0 EndX=116 EndY=7.5 EndZ=0
    g3: LineSegment StartX=116 StartY=7.5 StartZ=0 EndX=116 EndY=17.5 EndZ=0
  constraints (8):
    c: Coincident(g0,g1)
    c: Coincident(g1,g2)
    c: Coincident(g2,g3)
    c: Coincident(g3,g0)
    c: Horizontal(g0)
    c: Horizontal(g2)
    c: Vertical(g1)
    c: Vertical(g3)
FEATURE [Mesh::Feature] HexNutStyle1_M006  label="HexNutStyle1_M012"
  Placement = pos=(122.3,13.65,-114) rot=(0,0,1;0.523599rad)
FEATURE [PartDesign::Pad] Pad004
  Length = 15
  Length2 = 100
  Sketch = -> Sketch016
  Type = 0
FEATURE [Sketcher::SketchObject] Sketch017
  Placement = pos=(0,0,1.5) rot=(1,0,0;3.14159rad)
  Support = -> Pad004 [Face210]
  sketch-geometry (1):
    g0: Circle CenterX=121 CenterY=12.5 CenterZ=0 NormalX=0 NormalY=0 NormalZ=1 Radius=1.8
  constraints (1):
    c: Radius(g0) = 1.8
FEATURE [PartDesign::Pocket] Pocket013
  Length = 8
  Sketch = -> Sketch017
  Type = 0
FEATURE [Sketcher::SketchObject] Sketch018
  Placement = pos=(126,0,0) rot=(0.57735,0.57735,0.57735;2.0944rad)
  Support = -> Pocket013 [Face206]
  sketch-geometry (4):
    g0: LineSegment StartX=-15.5 StartY=5.25 StartZ=0 EndX=-9.5 EndY=5.25 EndZ=0
    g1: LineSegment StartX=-9.5 StartY=5.25 StartZ=0 EndX=-9.5 EndY=2.56276 EndZ=0
    g2: LineSegment StartX=-9.5 StartY=2.56276 StartZ=0 EndX=-15.5 EndY=2.56276 EndZ=0
    g3: LineSegment StartX=-15.5 StartY=2.56276 StartZ=0 EndX=-15.5 EndY=5.25 EndZ=0
  constraints (8):
    c: Coincident(g0,g1)
    c: Coincident(g1,g2)
    c: Coincident(g2,g3)
    c: Coincident(g3,g0)
    c: Horizontal(g0)
    c: Horizontal(g2)
    c: Vertical(g1)
    c: Vertical(g3)
FEATURE [PartDesign::Pocket] Pocket014
  Length = 8.5
  Sketch = -> Sketch018
  Type = 0
FEATURE [Mesh::Feature] HexNutStyle1_M007  label="HexNutStyle1_M013"
  Placement = pos=(-16,7.15,12.44) rot=(0.250563,0.935113,0.250563;1.63783rad)
FEATURE [Mesh::Feature] HexNutStyle1_M008  label="HexNutStyle1_M014"
  Placement = pos=(-16,20.15,12.44) rot=(0.250563,0.935113,0.250563;1.63783rad)
FEATURE [Mesh::Feature] HexNutStyle1_M009  label="HexNutStyle1_M017"
  Placement = pos=(22.5,7.15,12.44) rot=(0.250563,0.935113,0.250563;1.63783rad)
FEATURE [Mesh::Feature] HexNutStyle1_M010  label="HexNutStyle1_M018"
  Placement = pos=(22.5,20.15,12.44) rot=(0.250563,0.935113,0.250563;1.63783rad)
FEATURE [Sketcher::SketchObject] Sketch020
  Placement = pos=(149,0,0) rot=(0.57735,0.57735,0.57735;2.0944rad)
  Support = -> Pocket014 [Face18]
  sketch-geometry (2):
    g0: Circle CenterX=-19 CenterY=13.75 CenterZ=0 NormalX=0 NormalY=0 NormalZ=1 Radius=1.8
    g1: Circle CenterX=-6 CenterY=13.75 CenterZ=0 NormalX=0 NormalY=0 NormalZ=1 Radius=1.8
  constraints (2):
    c: Radius(g0) = 1.8
    c: Radius(g1) = 1.8
FEATURE [PartDesign::Pocket] Pocket015
  Length = 12.5
  Sketch = -> Sketch020
  Type = 0
FEATURE [Sketcher::SketchObject] Sketch021
  Placement = pos=(149,0,0) rot=(0.57735,0.57735,0.57735;2.0944rad)
  Support = -> Pocket015 [Face18]
  sketch-geometry (2):
    g0: Circle CenterX=-19 CenterY=13.75 CenterZ=0 NormalX=0 NormalY=0 NormalZ=1 Radius=3.3
    g1: Circle CenterX=-6 CenterY=13.75 CenterZ=0 NormalX=0 NormalY=0 NormalZ=1 Radius=3.3
  constraints (2):
    c: Radius(g0) = 3.3
    c: Radius(g1) = 3.3
FEATURE [PartDesign::Pocket] Pocket016
  Length = 6
  Sketch = -> Sketch021
  Type = 0
FEATURE [Sketcher::SketchObject] Sketch022
  Placement = pos=(93,0,0) rot=(0.57735,-0.57735,-0.57735;2.0944rad)
  Support = -> Pocket016 [Face19]
  sketch-geometry (2):
    g0: Circle CenterX=6 CenterY=13.75 CenterZ=0 NormalX=0 NormalY=0 NormalZ=1 Radius=1.8
    g1: Circle CenterX=19 CenterY=13.75 CenterZ=0 NormalX=0 NormalY=0 NormalZ=1 Radius=1.8
  constraints (2):
    c: Radius(g0) = 1.8
    c: Radius(g1) = 1.8
FEATURE [PartDesign::Pocket] Pocket017
  Length = 12.5
  Sketch = -> Sketch022
  Type = 0
FEATURE [Sketcher::SketchObject] Sketch023
  Placement = pos=(93,0,0) rot=(0.57735,-0.57735,-0.57735;2.0944rad)
  Support = -> Pocket017 [Face19]
  sketch-geometry (2):
    g0: Circle CenterX=6 CenterY=13.75 CenterZ=0 NormalX=0 NormalY=0 NormalZ=1 Radius=3.3
    g1: Circle CenterX=19 CenterY=13.75 CenterZ=0 NormalX=0 NormalY=0 NormalZ=1 Radius=3.3
  constraints (2):
    c: Radius(g0) = 3.3
    c: Radius(g1) = 3.3
FEATURE [PartDesign::Pocket] Pocket018
  Length = 6
  Sketch = -> Sketch023
  Type = 0
FEATURE [Sketcher::SketchObject] Sketch024
  Placement = pos=(0,0,18) rot=(0,0,1;0rad)
  Support = -> Pocket018 [Face205]
  sketch-geometry (16):
    g0: LineSegment StartX=141.5 StartY=-3 StartZ=0 EndX=138.75 EndY=-3 EndZ=0
    g1: LineSegment StartX=138.75 StartY=-3 StartZ=0 EndX=138.75 EndY=-9 EndZ=0
    g2: LineSegment StartX=138.75 StartY=-9 StartZ=0 EndX=141.5 EndY=-9 EndZ=0
    g3: LineSegment StartX=141.5 StartY=-9 StartZ=0 EndX=141.5 EndY=-3 EndZ=0
    g4: LineSegment StartX=141.5 StartY=-16 StartZ=0 EndX=138.75 EndY=-16 EndZ=0
    g5: LineSegment StartX=138.75 StartY=-16 StartZ=0 EndX=138.75 EndY=-22 EndZ=0
    g6: LineSegment StartX=138.75 StartY=-22 StartZ=0 EndX=141.5 EndY=-22 EndZ=0
    g7: LineSegment StartX=141.5 StartY=-22 StartZ=0 EndX=141.5 EndY=-16 EndZ=0
    g8: LineSegment StartX=100.5 StartY=-16 StartZ=0 EndX=103.25 EndY=-16 EndZ=0
    g9: LineSegment StartX=103.25 StartY=-16 StartZ=0 EndX=103.25 EndY=-22 EndZ=0
    g10: LineSegment StartX=103.25 StartY=-22 StartZ=0 EndX=100.5 EndY=-22 EndZ=0
    g11: LineSegment StartX=100.5 StartY=-22 StartZ=0 EndX=100.5 EndY=-16 EndZ=0
    g12: LineSegment StartX=100.5 StartY=-9 StartZ=0 EndX=103.25 EndY=-9 EndZ=0
    g13: LineSegment StartX=103.25 StartY=-9 StartZ=0 EndX=103.25 EndY=-3 EndZ=0
    g14: LineSegment StartX=103.25 StartY=-3 StartZ=0 EndX=100.5 EndY=-3 EndZ=0
    g15: LineSegment StartX=100.5 StartY=-3 StartZ=0 EndX=100.5 EndY=-9 EndZ=0
  constraints (32):
    c: Coincident(g0,g1)
    c: Coincident(g1,g2)
    c: Coincident(g2,g3)
    c: Coincident(g3,g0)
    c: Horizontal(g0)
    c: Horizontal(g2)
    c: Vertical(g1)
    c: Vertical(g3)
    c: Coincident(g4,g5)
    c: Coincident(g5,g6)
    c: Coincident(g6,g7)
    c: Coincident(g7,g4)
    c: Horizontal(g4)
    c: Horizontal(g6)
    c: Vertical(g5)
    c: Vertical(g7)
    c: Coincident(g8,g9)
    c: Coincident(g9,g10)
    c: Coincident(g10,g11)
    c: Coincident(g11,g8)
    c: Horizontal(g8)
    c: Horizontal(g10)
    c: Vertical(g9)
    c: Vertical(g11)
    c: Coincident(g12,g13)
    c: Coincident(g13,g14)
    c: Coincident(g14,g15)
    c: Coincident(g15,g12)
    c: Horizontal(g12)
    c: Horizontal(g14)
    c: Vertical(g13)
    c: Vertical(g15)
FEATURE [PartDesign::Pocket] Pocket019
  Length = 8.5
  Sketch = -> Sketch024
  Type = 0
FEATURE [Sketcher::SketchObject] Sketch025
  Placement = pos=(0,0,6.5) rot=(1,0,0;3.14159rad)
  Support = -> Pocket019 [Face188]
  sketch-geometry (4):
    g0: LineSegment StartX=104.25 StartY=13.5 StartZ=0 EndX=94.5 EndY=13.5 EndZ=0
    g1: LineSegment StartX=94.5 StartY=13.5 StartZ=0 EndX=94.5 EndY=11.5 EndZ=0
    g2: LineSegment StartX=94.5 StartY=11.5 StartZ=0 EndX=104.25 EndY=11.5 EndZ=0
    g3: LineSegment StartX=104.25 StartY=11.5 StartZ=0 EndX=104.25 EndY=13.5 EndZ=0
  constraints (8):
    c: Coincident(g0,g1)
    c: Coincident(g1,g2)
    c: Coincident(g2,g3)
    c: Coincident(g3,g0)
    c: Horizontal(g0)
    c: Horizontal(g2)
    c: Vertical(g1)
    c: Vertical(g3)
FEATURE [PartDesign::Pad] Pad005
  Length = 5
  Length2 = 100
  Sketch = -> Sketch025
  Type = 0
FEATURE [PartDesign::Fillet] Fillet009
  Base = -> Pad005 [Edge738,Edge726]
  Radius = 0.9
FEATURE [PartDesign::Fillet] Fillet010
  Base = -> Fillet009 [Edge535,Edge538,Edge537,Edge544]
  Radius = 1.5
FEATURE [Sketcher::SketchObject] Sketch026
  Placement = pos=(0,0,1.5) rot=(1,0,0;3.14159rad)
  Support = -> Fillet010 [Face74]
  sketch-geometry (2):
    g0: Circle CenterX=121 CenterY=43 CenterZ=0 NormalX=0 NormalY=0 NormalZ=1 Radius=1.8
    g1: Circle CenterX=121 CenterY=-18 CenterZ=0 NormalX=0 NormalY=0 NormalZ=1 Radius=1.8
  constraints (2):
    c: Radius(g1) = 1.8
    c: Radius(g0) = 1.8
FEATURE [PartDesign::Pocket] Pocket020
  Length = 5
  Sketch = -> Sketch026
  Type = 0
FEATURE [Part::Feature] Pocket021  label="XCarrageTop"
  shape: bbox 56 x 70.62 x 16.52 mm, 278 faces (baked)
